# Revit family: Sanitary_Taps-mixers_hansgrohe_74711XXX-Zesis-S-Single-lever-basin-mixer-70_CoolStart_no-waste-set
name_source: partatom
category: Plumbing Fixtures
units: mm (PartAtom-declared; Revit-internal decimal feet)

## family parameters
Always vertical = No
Cut with Voids When Loaded = No
Maintain Annotation Orientation = No
OmniClass Number = 23.31.11.00
OmniClass Title = Faucets
Part Type = Normal
Room Calculation Point = No
Round Connector Dimension = Use Diameter
Shared = No
Work Plane-Based = Yes

## types (1)
- 000 Chrome
    Connector Description = Water Inlet 9.5 mm
    Default Elevation = 0 mm  [stored 0 ft]
    Description = Zesis S Single lever basin mixer 70 CoolStart without waste set
    Diameter = 9.5 mm  [stored 0.031168 ft]
    Manufacturer = Hansgrohe
    Material 1 = Hansgrohe - Metal - 000 Chrome
    Model = 74711XXX
    Product Page URL = https://www.hansgrohe.com
    Product data url = https://www.bimobject.com
    URL = https://www.hansgrohe.com
    Version = 1

note: [stored X ft] marks values corroborated as IEEE doubles in the binary element streams (Revit-internal decimal feet)

## geometry (parser evidence)
native form markers: Sweep x2
no freeform markers — native parametric forms only
